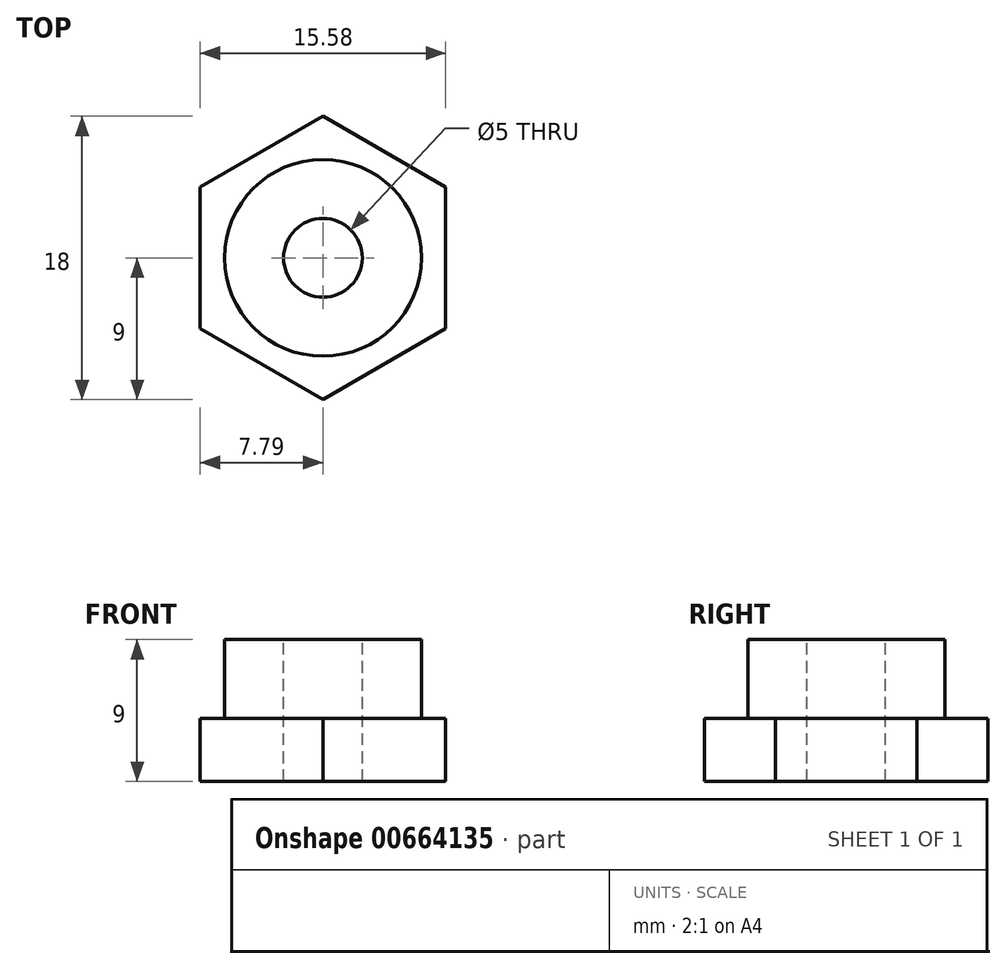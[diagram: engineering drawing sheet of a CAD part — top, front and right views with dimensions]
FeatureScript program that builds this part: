
annotation { "Feature Type Name" : "Feature", "Feature Type Description" : "" }
export const myFeature = defineFeature(function(context is Context, id is Id, definition is map)
    precondition{}
    {
        {
            var Q0;
            Q0=qCreatedBy(makeId("Top.planeOp"),FACE);
            var sketch = newSketch(context, id + "F0", { "sketchPlane" : qUnion([Q0])});
            skCircle(sketch, "E0.cCircle", {"center": v(0, 0) * mm, "radius": 7.8 * mm, "construction": true});
            skLineSegment(sketch, "E0.0", {"start": v(-7.8, -4.5) * mm, "end": v(-7.8, 4.5) * mm});
            skLineSegment(sketch, "E0.1", {"start": v(-7.8, 4.5) * mm, "end": v(0, 9) * mm});
            skLineSegment(sketch, "E0.2", {"start": v(0, 9) * mm, "end": v(7.8, 4.5) * mm});
            skLineSegment(sketch, "E0.3", {"start": v(7.8, 4.5) * mm, "end": v(7.8, -4.5) * mm});
            skLineSegment(sketch, "E0.4", {"start": v(7.8, -4.5) * mm, "end": v(0, -9) * mm});
            skLineSegment(sketch, "E0.5", {"start": v(0, -9) * mm, "end": v(-7.8, -4.5) * mm});
            skPoint(sketch, "E0.0.midPoint", {"position": v(-7.8, 0) * mm});
            skSolve(sketch);
        }
        {
            var Q0;
            Q0=qCreatedBy(makeId("Top.planeOp"),FACE);
            var sketch = newSketch(context, id + "F1", { "sketchPlane" : qUnion([Q0])});
            skCircle(sketch, "E1", {"center": v(0, 0) * mm, "radius": 6.25 * mm});
            skSolve(sketch);
        }
        {
            var Q0;
            Q0=makeQuery(id+"F0.imprint","IMPRINT",FACE,{"disambiguationData":[TD([[makeQuery(id+"F0.imprint","IMPRINT",EDGE,{"derivedFrom":sQuery(id+"F0.wireOp",EDGE,"E0.0")}),-1.0]])]});
            extrude(context, id + "F2", {"entities" : qUnion([Q0]), "depth" : 4 * mm, "offsetDistance" : 25 * mm});
        }
        {
            var Q0;
            Q0=qSketchRegion(id+"F1",true);
            extrude(context, id + "F3", {"entities" : qUnion([Q0]), "operationType" : NewBodyOperationType.ADD, "depth" : 9 * mm, "offsetDistance" : 25 * mm});
        }
        {
            var Q0;
            Q0=makeQuery(id+"F3.opExtrude","CAP_FACE",FACE,{"disambiguationData":[OSD([sQuery(id+"F1.wireOp",EDGE,"E1")])],"isStart":false});
            var sketch = newSketch(context, id + "F4", { "sketchPlane" : qUnion([Q0])});
            skLineSegment(sketch, "E2", {"start": v(-0.55, 0) * mm, "end": v(0, 0) * mm});
            skSolve(sketch);
        }
        {
            var Q0;
            Q0=sQuery(id+"F4.wireOp",VERTEX,"E2.end");
            var Q1;
            Q1=makeQuery(id+"F2.opExtrude","SWEPT_BODY",BODY,{"disambiguationData":[OSD([sQuery(id+"F0.wireOp",EDGE,"E0.0"),sQuery(id+"F0.wireOp",EDGE,"E0.1"),sQuery(id+"F0.wireOp",EDGE,"E0.2"),sQuery(id+"F0.wireOp",EDGE,"E0.3"),sQuery(id+"F0.wireOp",EDGE,"E0.4"),sQuery(id+"F0.wireOp",EDGE,"E0.5")])]});
            hole(context, id + "F5", {"style" : HoleStyle.SIMPLE, "endStyle" : HoleEndStyle.THROUGH, "holeDiameter" : 5 * mm, "majorDiameter" : 5 * mm, "isTappedThrough" : true, "tappedDepth" : 12 * mm, "tapClearance" : 3, "locations" : qUnion([Q0]), "scope" : qUnion([Q1])});
        }
    });
